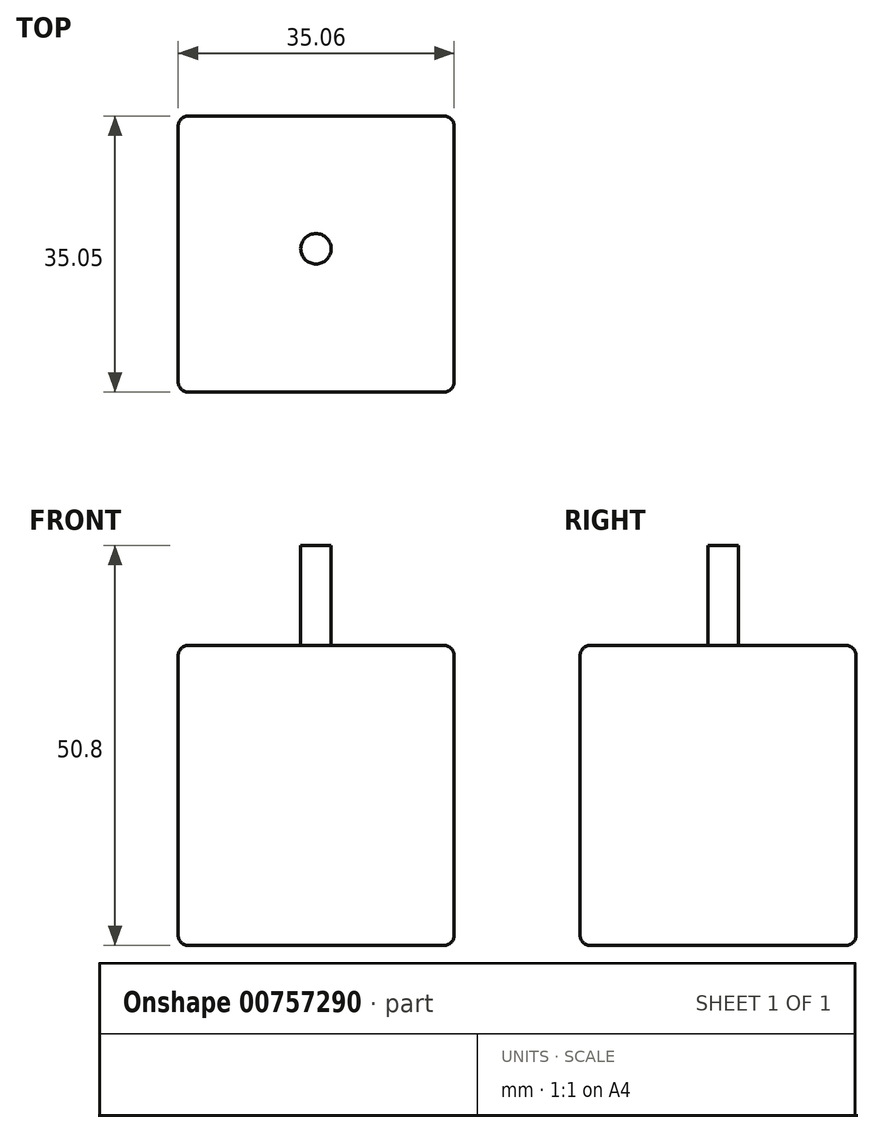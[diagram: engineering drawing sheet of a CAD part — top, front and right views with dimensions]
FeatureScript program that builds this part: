
annotation { "Feature Type Name" : "Feature", "Feature Type Description" : "" }
export const myFeature = defineFeature(function(context is Context, id is Id, definition is map)
    precondition{}
    {
        {
            var Q0;
            Q0=qCreatedBy(makeId("Top.planeOp"),FACE);
            var sketch = newSketch(context, id + "F0", { "sketchPlane" : qUnion([Q0])});
            skLineSegment(sketch, "E0.bottom", {"start": v(-41.09, 37.53) * mm, "end": v(-6.03, 37.53) * mm});
            skLineSegment(sketch, "E0.top", {"start": v(-41.09, 2.48) * mm, "end": v(-6.03, 2.48) * mm});
            skLineSegment(sketch, "E0.left", {"start": v(-41.09, 37.53) * mm, "end": v(-41.09, 2.48) * mm});
            skLineSegment(sketch, "E0.right", {"start": v(-6.03, 37.53) * mm, "end": v(-6.03, 2.48) * mm});
            skSolve(sketch);
        }
        {
            var Q0;
            Q0 = qSketchRegion(id + "F0", true);
            extrude(context, id + "F1", {"entities" : qUnion([Q0]), "depth" : 38.1 * mm, "offsetDistance" : 25.4 * mm});
        }
        {
            var Q0;
            Q0=qCreatedBy(makeId("Top.planeOp"),FACE);
            var sketch = newSketch(context, id + "F2", { "sketchPlane" : qUnion([Q0])});
            skCircle(sketch, "E1", {"center": v(-23.59, 20.67) * mm, "radius": 1.93 * mm});
            skSolve(sketch);
        }
        {
            var Q0;
            Q0 = qSketchRegion(id + "F2", true);
            extrude(context, id + "F3", {"entities" : qUnion([Q0]), "operationType" : NewBodyOperationType.ADD, "depth" : 50.8 * mm, "offsetDistance" : 25.4 * mm});
        }
        {
            var Q0;
            Q0=makeQuery(id+"F1.opExtrude","CAP_EDGE",EDGE,{"disambiguationData":[OSD([sQuery(id+"F0.wireOp",EDGE,"E0.bottom")])],"isStart":false});
            var Q1;
            Q1=makeQuery(id+"F1.opExtrude","SWEPT_FACE",FACE,{"disambiguationData":[OSD([sQuery(id+"F0.wireOp",EDGE,"E0.left")])]});
            var Q2;
            Q2=makeQuery(id+"F1.opExtrude","CAP_EDGE",EDGE,{"disambiguationData":[OSD([sQuery(id+"F0.wireOp",EDGE,"E0.top")])],"isStart":false});
            var Q3;
            Q3=makeQuery(id+"F1.opExtrude","CAP_EDGE",EDGE,{"disambiguationData":[OSD([sQuery(id+"F0.wireOp",EDGE,"E0.right")])],"isStart":false});
            var Q4;
            Q4=makeQuery(id+"F1.opExtrude","SWEPT_EDGE",EDGE,{"disambiguationData":[OSD([sQuery(id+"F0.wireOp",EDGE,"E0.top"),sQuery(id+"F0.wireOp",EDGE,"E0.right")])]});
            var Q5;
            Q5=makeQuery(id+"F1.opExtrude","SWEPT_FACE",FACE,{"disambiguationData":[OSD([sQuery(id+"F0.wireOp",EDGE,"E0.top")])]});
            var Q6;
            Q6=makeQuery(id+"F1.opExtrude","SWEPT_FACE",FACE,{"disambiguationData":[OSD([sQuery(id+"F0.wireOp",EDGE,"E0.right")])]});
            var Q7;
            Q7=makeQuery(id+"F1.opExtrude","CAP_FACE",FACE,{"disambiguationData":[OSD([sQuery(id+"F0.wireOp",EDGE,"E0.bottom"),sQuery(id+"F0.wireOp",EDGE,"E0.top"),sQuery(id+"F0.wireOp",EDGE,"E0.left"),sQuery(id+"F0.wireOp",EDGE,"E0.right")])],"isStart":true});
            fillet(context, id + "F4", {"entities" : qUnion([Q0, Q1, Q2, Q3, Q4, Q5, Q6, Q7]), "radius" : 1.27 * mm, "tangentPropagation" : true, "allowEdgeOverflow" : false});
        }
    });
